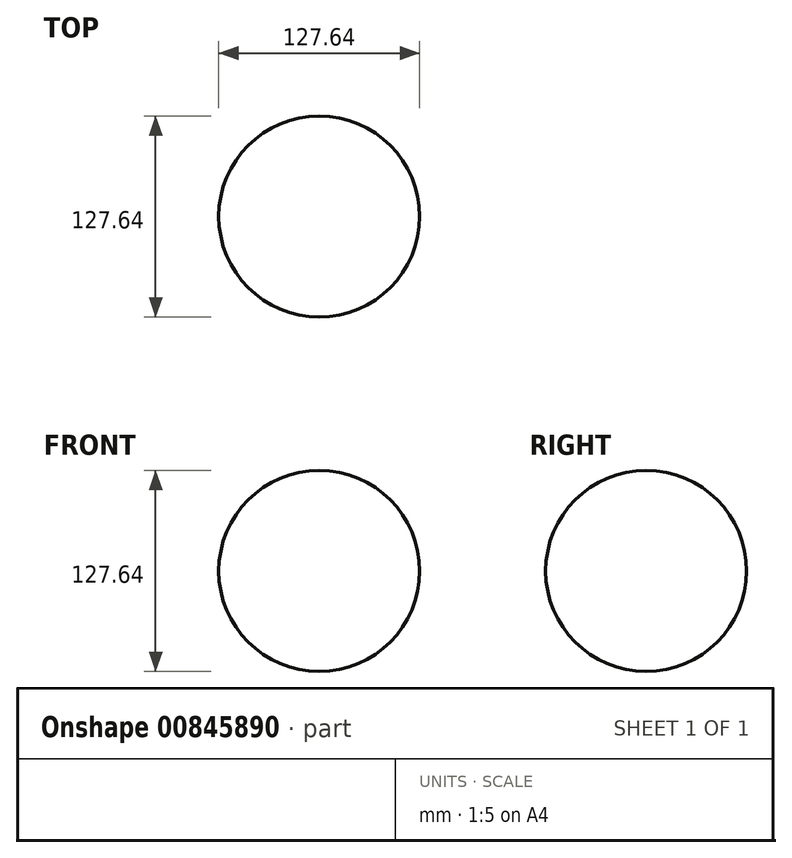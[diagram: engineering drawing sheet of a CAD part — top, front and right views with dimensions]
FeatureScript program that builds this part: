
annotation { "Feature Type Name" : "Feature", "Feature Type Description" : "" }
export const myFeature = defineFeature(function(context is Context, id is Id, definition is map)
    precondition{}
    {
        {
            var Q0;
            Q0=qCreatedBy(makeId("Front.planeOp"),FACE);
            var sketch = newSketch(context, id + "F0", { "sketchPlane" : qUnion([Q0])});
            skCircle(sketch, "E0", {"center": v(0, 0) * mm, "radius": 63.82 * mm});
            skLineSegment(sketch, "E1", {"start": v(0, 77.2) * mm, "end": v(0, -75.87) * mm});
            skSolve(sketch);
        }
        {
            var Q0;
            {var subQ0=sQuery(id+"F0.wireOp",EDGE,"E1");var subQ1=sQuery(id+"F0.wireOp",EDGE,"E0");var subQ2=makeQuery(id+"F0.imprint","INTERSECT",VERTEX,{"disambiguationData":[OD(0.0)],"derivedFrom":[subQ1,subQ0]});Q0=makeQuery(id+"F0.imprint","IMPRINT",FACE,{"disambiguationData":[TD([[makeQuery(id+"F0.imprint","IMPRINT",EDGE,{"disambiguationData":[TD([[subQ2,-1.0]])],"derivedFrom":subQ1}),1.0]])]});}
            var Q1;
            Q1=sQuery(id+"F0.wireOp",EDGE,"E1");
            revolve(context, id + "F1", {"surfaceOperationType" : NewSurfaceOperationType.NEW, "entities" : qUnion([Q0]), "axis" : qUnion([Q1]), "revolveType" : RevolveType.FULL});
        }
    });
